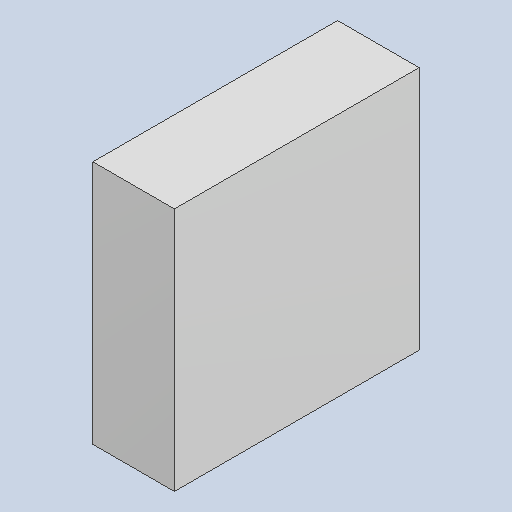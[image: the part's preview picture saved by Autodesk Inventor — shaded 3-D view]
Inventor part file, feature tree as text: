
AUTODESK INVENTOR PART (.ipt)
format: ipt  version: 2023.4 (Build 274418000, 418)  size: 81,408 bytes
history: native  units: mm
features: extrude x1
ambient origin geometry x8: Origin, YZ Plane, XZ Plane, XY Plane, X Axis, Y Axis, Z Axis, Center Point
bodies: Solid1 (feature_tree)
feature tree (1):
  extrude  "Extruded_10"  [1 undecoded]
note: 1 required parameter value undecoded (feature->parameter linkage not recoverable at this tier; creation-order binding heuristic only, values carry confidence <= 0.55)
